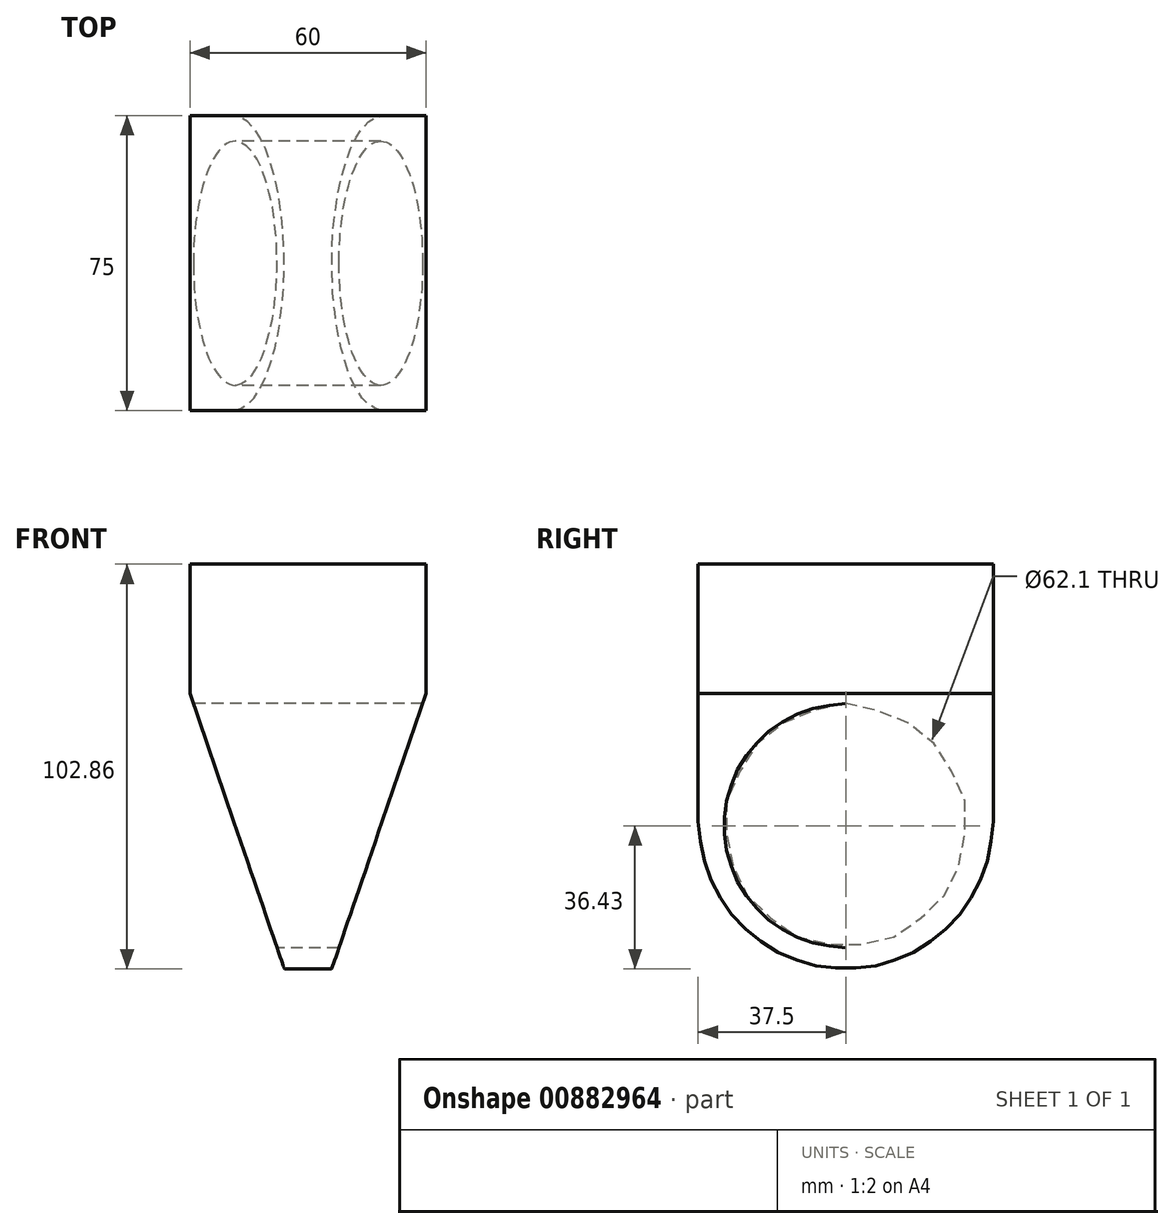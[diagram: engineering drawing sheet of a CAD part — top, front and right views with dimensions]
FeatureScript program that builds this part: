
annotation { "Feature Type Name" : "Feature", "Feature Type Description" : "" }
export const myFeature = defineFeature(function(context is Context, id is Id, definition is map)
    precondition{}
    {
        {
            var Q0;
            Q0=qCreatedBy(makeId("Right.planeOp"),FACE);
            var sketch = newSketch(context, id + "F0", { "sketchPlane" : qUnion([Q0])});
            skCircle(sketch, "E0", {"center": v(0, 0) * mm, "radius": 31.05 * mm});
            skLineSegment(sketch, "E1.bottom", {"start": v(-37.5, -36.43) * mm, "end": v(37.5, -36.43) * mm});
            skLineSegment(sketch, "E1.top", {"start": v(-37.5, 36.43) * mm, "end": v(37.5, 36.43) * mm});
            skLineSegment(sketch, "E1.left", {"start": v(-37.5, -36.43) * mm, "end": v(-37.5, 36.43) * mm});
            skLineSegment(sketch, "E1.right", {"start": v(37.5, -36.43) * mm, "end": v(37.5, 36.43) * mm});
            skLineSegment(sketch, "E2.top", {"start": v(-37.5, 66.43) * mm, "end": v(37.5, 66.43) * mm});
            skLineSegment(sketch, "E2.left", {"start": v(-37.5, 36.43) * mm, "end": v(-37.5, 66.43) * mm});
            skLineSegment(sketch, "E2.right", {"start": v(37.5, 36.43) * mm, "end": v(37.5, 66.43) * mm});
            skSolve(sketch);
        }
        {
            var Q0;
            Q0=makeQuery(id+"F0.imprint","IMPRINT",FACE,{"disambiguationData":[TD([[makeQuery(id+"F0.imprint","IMPRINT",EDGE,{"derivedFrom":sQuery(id+"F0.wireOp",EDGE,"E1.top")}),1.0]])]});
            var Q1;
            Q1=makeQuery(id+"F0.imprint","IMPRINT",FACE,{"disambiguationData":[TD([[makeQuery(id+"F0.imprint","IMPRINT",EDGE,{"derivedFrom":sQuery(id+"F0.wireOp",EDGE,"E0")}),-1.0]])]});
            extrude(context, id + "F1", {"entities" : qUnion([Q0, Q1]), "endBound" : BoundingType.SYMMETRIC, "depth" : 60 * mm, "offsetDistance" : 25 * mm});
        }
        {
            var Q0;
            Q0=makeQuery(id+"F1.opExtrude","CAP_EDGE",EDGE,{"disambiguationData":[OSD([sQuery(id+"F0.wireOp",EDGE,"E1.bottom")])],"isStart":false});
            var Q1;
            Q1=makeQuery(id+"F1.opExtrude","CAP_EDGE",EDGE,{"disambiguationData":[OSD([sQuery(id+"F0.wireOp",EDGE,"E1.bottom")])],"isStart":true});
            chamfer(context, id + "F2", {"entities" : qUnion([Q0, Q1]), "chamferType" : ChamferType.TWO_OFFSETS, "width1" : 70 * mm, "oppositeDirection" : false, "width2" : 24 * mm, "tangentPropagation" : true});
        }
        {
            var Q0;
            Q0=makeQuery(id+"F1.opExtrude","SWEPT_EDGE",EDGE,{"disambiguationData":[OSD([sQuery(id+"F0.wireOp",EDGE,"E1.bottom"),sQuery(id+"F0.wireOp",EDGE,"E1.left")])]});
            var Q1;
            Q1=makeQuery(id+"F1.opExtrude","SWEPT_EDGE",EDGE,{"disambiguationData":[OSD([sQuery(id+"F0.wireOp",EDGE,"E1.bottom"),sQuery(id+"F0.wireOp",EDGE,"E1.right")])]});
            fillet(context, id + "F3", {"entities" : qUnion([Q0, Q1]), "radius" : 37.5 * mm, "tangentPropagation" : true, "allowEdgeOverflow" : false});
        }
    });
